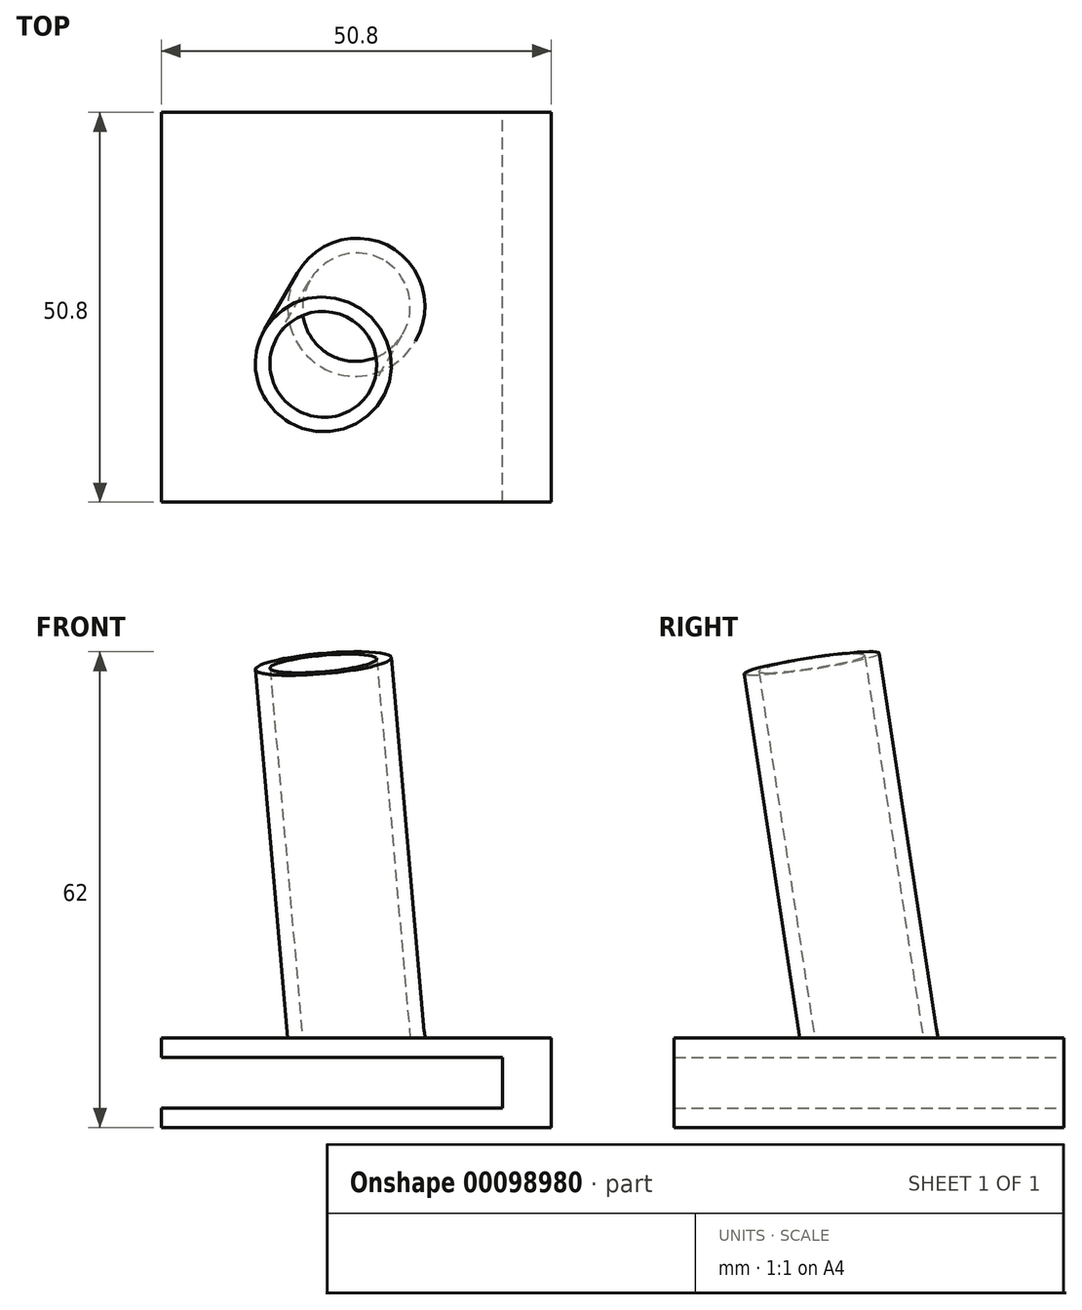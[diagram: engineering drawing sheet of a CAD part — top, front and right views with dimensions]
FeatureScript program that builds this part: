
annotation { "Feature Type Name" : "Feature", "Feature Type Description" : "" }
export const myFeature = defineFeature(function(context is Context, id is Id, definition is map)
    precondition{}
    {
        {
            var Q0;
            Q0=qCreatedBy(makeId("Top.planeOp"),FACE);
            var sketch = newSketch(context, id + "F0", { "sketchPlane" : qUnion([Q0])});
            skLineSegment(sketch, "E0.bottom", {"start": v(25.4, 25.4) * mm, "end": v(-25.4, 25.4) * mm});
            skLineSegment(sketch, "E0.top", {"start": v(25.4, -25.4) * mm, "end": v(-25.4, -25.4) * mm});
            skLineSegment(sketch, "E0.left", {"start": v(25.4, 25.4) * mm, "end": v(25.4, -25.4) * mm});
            skLineSegment(sketch, "E0.right", {"start": v(-25.4, 25.4) * mm, "end": v(-25.4, -25.4) * mm});
            skPoint(sketch, "E0.middle", {"position": v(0, 0) * mm});
            skSolve(sketch);
        }
        {
            var Q0;
            Q0 = qSketchRegion(id + "F0", true);
            extrude(context, id + "F1", {"entities" : qUnion([Q0]), "oppositeDirection" : true, "depth" : 2.54 * mm});
        }
        {
            var Q0;
            Q0=makeQuery(id+"F1.opExtrude","CAP_FACE",FACE,{"disambiguationData":[OSD([sQuery(id+"F0.wireOp",EDGE,"E0.bottom"),sQuery(id+"F0.wireOp",EDGE,"E0.top"),sQuery(id+"F0.wireOp",EDGE,"E0.left"),sQuery(id+"F0.wireOp",EDGE,"E0.right")])],"isStart":false});
            var sketch = newSketch(context, id + "F2", { "sketchPlane" : qUnion([Q0])});
            skLineSegment(sketch, "E1.bottom", {"start": v(25.4, 25.4) * mm, "end": v(19.05, 25.4) * mm});
            skLineSegment(sketch, "E1.top", {"start": v(25.4, -25.4) * mm, "end": v(19.05, -25.4) * mm});
            skLineSegment(sketch, "E1.left", {"start": v(25.4, 25.4) * mm, "end": v(25.4, -25.4) * mm});
            skLineSegment(sketch, "E1.right", {"start": v(19.05, 25.4) * mm, "end": v(19.05, -25.4) * mm});
            skSolve(sketch);
        }
        {
            var Q0;
            Q0 = qSketchRegion(id + "F2", true);
            extrude(context, id + "F3", {"entities" : qUnion([Q0]), "operationType" : NewBodyOperationType.ADD, "depth" : 6.6 * mm});
        }
        {
            var Q0;
            Q0=makeQuery(id+"F3.opExtrude","CAP_FACE",FACE,{"disambiguationData":[OSD([sQuery(id+"F2.wireOp",EDGE,"E1.bottom"),sQuery(id+"F2.wireOp",EDGE,"E1.top"),sQuery(id+"F2.wireOp",EDGE,"E1.left"),sQuery(id+"F2.wireOp",EDGE,"E1.right")])],"isStart":false});
            var sketch = newSketch(context, id + "F4", { "sketchPlane" : qUnion([Q0])});
            skLineSegment(sketch, "E2.bottom", {"start": v(25.4, 25.4) * mm, "end": v(-25.4, 25.4) * mm});
            skLineSegment(sketch, "E2.top", {"start": v(25.4, -25.4) * mm, "end": v(-25.4, -25.4) * mm});
            skLineSegment(sketch, "E2.left", {"start": v(25.4, 25.4) * mm, "end": v(25.4, -25.4) * mm});
            skLineSegment(sketch, "E2.right", {"start": v(-25.4, 25.4) * mm, "end": v(-25.4, -25.4) * mm});
            skSolve(sketch);
        }
        {
            var Q0;
            Q0 = qSketchRegion(id + "F4", true);
            extrude(context, id + "F5", {"entities" : qUnion([Q0]), "operationType" : NewBodyOperationType.ADD, "depth" : 2.54 * mm});
        }
        {
            var Q0;
            Q0=makeQuery(id+"F1.opExtrude","CAP_FACE",FACE,{"disambiguationData":[OSD([sQuery(id+"F0.wireOp",EDGE,"E0.bottom"),sQuery(id+"F0.wireOp",EDGE,"E0.top"),sQuery(id+"F0.wireOp",EDGE,"E0.left"),sQuery(id+"F0.wireOp",EDGE,"E0.right")])],"isStart":true});
            var sketch = newSketch(context, id + "F6", { "sketchPlane" : qUnion([Q0])});
            skLineSegment(sketch, "E3", {"start": v(0, 25.4) * mm, "end": v(0, -28.09) * mm, "construction": true});
            skPoint(sketch, "E3.endSnap0", {"position": v(0, -25.4) * mm});
            skSolve(sketch);
        }
        {
            var Q0;
            Q0=qCreatedBy(makeId("Right.planeOp"),FACE);
            var sketch = newSketch(context, id + "F7", { "sketchPlane" : qUnion([Q0])});
            skLineSegment(sketch, "E4", {"start": v(0, 55.88) * mm, "end": v(0, -47.56) * mm, "construction": true});
            skSolve(sketch);
        }
        {
            var Q0;
            Q0=sQuery(id+"F6.wireOp",EDGE,"E3");
            cPlane(context, id + "F8", {"entities" : qUnion([Q0]), "cplaneType" : CPlaneType.LINE_ANGLE, "offset" : 152.4 * mm, "angle" : 10 * degree, "width" : 152.4 * mm, "height" : 152.4 * mm});
        }
        {
            var Q0;
            Q0=qCreatedBy(id+"F8.planeOp",FACE);
            var sketch = newSketch(context, id + "F9", { "sketchPlane" : qUnion([Q0])});
            skCircle(sketch, "E5", {"center": v(0, 0) * mm, "radius": 6.99 * mm});
            skCircle(sketch, "E6", {"center": v(0, 0) * mm, "radius": 8.9 * mm});
            skSolve(sketch);
        }
        {
            var Q0;
            Q0 = qSketchRegion(id + "F9", true);
            extrude(context, id + "F10", {"entities" : qUnion([Q0]), "oppositeDirection" : true, "depth" : 49.53 * mm});
        }
        {
            var Q0;
            Q0=makeQuery(id+"F10.opExtrude","SWEPT_BODY",BODY,{"disambiguationData":[OSD([sQuery(id+"F9.wireOp",EDGE,"E5"),sQuery(id+"F9.wireOp",EDGE,"E6")])]});
            var Q1;
            Q1=sQuery(id+"F7.wireOp",EDGE,"E4");
            transform(context, id + "F11", {"entities" : qUnion([Q0]), "transformType" : TransformType.ROTATION, "transformAxis" : qUnion([Q1]), "angle" : 60 * degree, "oppositeDirection" : true, "makeCopy" : false});
        }
        {
            var Q0;
            Q0=qCreatedBy(makeId("Top.planeOp"),FACE);
            var sketch = newSketch(context, id + "F12", { "sketchPlane" : qUnion([Q0])});
            skLineSegment(sketch, "E7", {"start": v(-54.24, 36.53) * mm, "end": v(-54.24, -61.05) * mm, "construction": true});
            skSolve(sketch);
        }
        {
            var Q0;
            Q0=qCreatedBy(makeId("Right.planeOp"),FACE);
            var sketch = newSketch(context, id + "F13", { "sketchPlane" : qUnion([Q0])});
            skLineSegment(sketch, "E8", {"start": v(8.85, -52.8) * mm, "end": v(8.85, 70.73) * mm, "construction": true});
            skSolve(sketch);
        }
        {
            var Q0;
            Q0=makeQuery(id+"F10.opExtrude","CAP_FACE",FACE,{"disambiguationData":[OSD([sQuery(id+"F9.wireOp",EDGE,"E5"),sQuery(id+"F9.wireOp",EDGE,"E6")])],"isStart":false});
            var sketch = newSketch(context, id + "F14", { "sketchPlane" : qUnion([Q0])});
            skCircle(sketch, "E9", {"center": v(0, 0) * mm, "radius": 6.99 * mm});
            skCircle(sketch, "E10", {"center": v(0, 0) * mm, "radius": 8.9 * mm});
            skSolve(sketch);
        }
        {
            var Q0;
            Q0 = qSketchRegion(id + "F14", true);
            var Q1;
            Q1=sQuery(id+"F14.wireOp",EDGE,"E10");
            var Q2;
            Q2=makeQuery(id+"F1.opExtrude","CAP_FACE",FACE,{"disambiguationData":[OSD([sQuery(id+"F0.wireOp",EDGE,"E0.bottom"),sQuery(id+"F0.wireOp",EDGE,"E0.top"),sQuery(id+"F0.wireOp",EDGE,"E0.left"),sQuery(id+"F0.wireOp",EDGE,"E0.right")])],"isStart":true});
            extrude(context, id + "F15", {"entities" : qUnion([Q0]), "operationType" : NewBodyOperationType.ADD, "surfaceEntities" : qUnion([Q1]), "endBound" : BoundingType.UP_TO_SURFACE, "oppositeDirection" : true, "endBoundEntityFace" : qUnion([Q2]), "depth" : 25.4 * mm});
        }
    });
